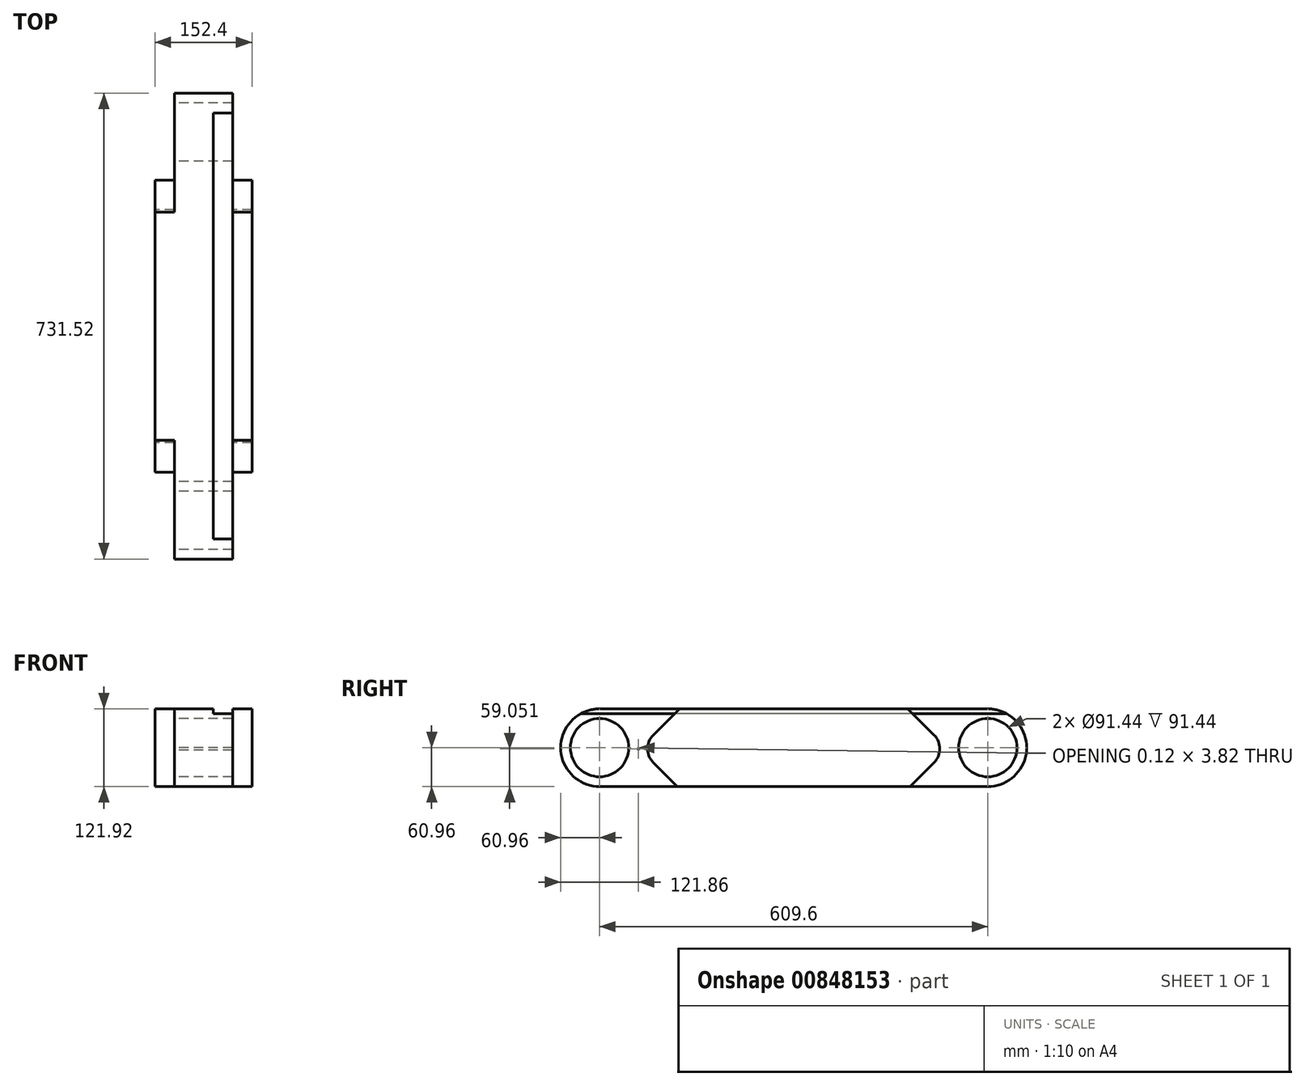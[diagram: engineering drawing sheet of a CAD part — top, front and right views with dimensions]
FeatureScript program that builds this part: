
annotation { "Feature Type Name" : "Feature", "Feature Type Description" : "" }
export const myFeature = defineFeature(function(context is Context, id is Id, definition is map)
    precondition{}
    {
        {
            var Q0;
            Q0=qCreatedBy(makeId("Right.planeOp"),FACE);
            var sketch = newSketch(context, id + "F0", { "sketchPlane" : qUnion([Q0])});
            skCircle(sketch, "E0", {"center": v(0, 0) * mm, "radius": 45.72 * mm});
            skCircle(sketch, "E1", {"center": v(0, 0) * mm, "radius": 60.96 * mm});
            skLineSegment(sketch, "E2.bottom", {"start": v(0, 60.96) * mm, "end": v(-609.6, 60.96) * mm});
            skLineSegment(sketch, "E2.top", {"start": v(0, -60.96) * mm, "end": v(-609.6, -60.96) * mm});
            skLineSegment(sketch, "E2.left", {"start": v(0, 60.96) * mm, "end": v(0, -60.96) * mm});
            skLineSegment(sketch, "E2.right", {"start": v(-609.6, 60.96) * mm, "end": v(-609.6, -60.96) * mm});
            skCircle(sketch, "E3", {"center": v(-609.6, 0) * mm, "radius": 60.96 * mm});
            skCircle(sketch, "E4", {"center": v(-609.6, 0) * mm, "radius": 45.72 * mm});
            skLineSegment(sketch, "E5", {"start": v(-60.96, 0) * mm, "end": v(-60.96, 60.96) * mm});
            skLineSegment(sketch, "E6", {"start": v(-548.64, 0) * mm, "end": v(-548.64, -60.96) * mm});
            skLineSegment(sketch, "E7", {"start": v(-548.76, -3.82) * mm, "end": v(-483.98, 60.96) * mm});
            skLineSegment(sketch, "E8", {"start": v(-548.64, 0) * mm, "end": v(-487.68, -60.96) * mm});
            skLineSegment(sketch, "E9", {"start": v(-304.8, 60.96) * mm, "end": v(-304.8, -60.96) * mm});
            skLineSegment(sketch, "E10.MirrorCS", {"start": v(-60.84, -3.82) * mm, "end": v(-125.62, 60.96) * mm});
            skLineSegment(sketch, "E11.MirrorCS", {"start": v(-60.96, 0) * mm, "end": v(-121.92, -60.96) * mm});
            skSolve(sketch);
        }
        {
            var Q0;
            Q0 = qSketchRegion(id + "F0", true);
            var Q1;
            {var subQ1=sQuery(id+"F0.wireOp",EDGE,"E6");var subQ3=sQuery(id+"F0.wireOp",EDGE,"E7");var subQ4=makeQuery(id+"F0.imprint","INTERSECT",VERTEX,{"derivedFrom":[subQ1,subQ3]});Q1=makeQuery(id+"F0.imprint","IMPRINT",FACE,{"disambiguationData":[TD([[makeQuery(id+"F0.imprint","IMPRINT",EDGE,{"disambiguationData":[TD([[subQ4,-1.0]])],"derivedFrom":subQ3}),1.0]])]});}
            var Q2;
            {var subQ1=sQuery(id+"F0.wireOp",EDGE,"E1");var subQ3=sQuery(id+"F0.wireOp",EDGE,"E10.MirrorCS");var subQ4=makeQuery(id+"F0.imprint","INTERSECT",VERTEX,{"derivedFrom":[subQ1,subQ3]});Q2=makeQuery(id+"F0.imprint","IMPRINT",FACE,{"disambiguationData":[TD([[makeQuery(id+"F0.imprint","IMPRINT",EDGE,{"disambiguationData":[TD([[subQ4,-1.0]])],"derivedFrom":subQ3}),-1.0]])]});}
            extrude(context, id + "F1", {"entities" : qUnion([Q0, Q1, Q2]), "depth" : 91.44 * mm, "offsetDistance" : 30.48 * mm, "symmetric" : true});
        }
        {
            var Q0;
            Q0=qCreatedBy(makeId("Front.planeOp"),FACE);
            var sketch = newSketch(context, id + "F2", { "sketchPlane" : qUnion([Q0])});
            skLineSegment(sketch, "E12.bottom", {"start": v(76.2, 60.96) * mm, "end": v(-76.2, 60.96) * mm});
            skLineSegment(sketch, "E12.top", {"start": v(76.2, -60.96) * mm, "end": v(-76.2, -60.96) * mm});
            skLineSegment(sketch, "E12.left", {"start": v(76.2, 60.96) * mm, "end": v(76.2, -60.96) * mm});
            skLineSegment(sketch, "E12.right", {"start": v(-76.2, 60.96) * mm, "end": v(-76.2, -60.96) * mm});
            skPoint(sketch, "E12.middle", {"position": v(0, 0) * mm});
            skLineSegment(sketch, "E13.bottom", {"start": v(-45.72, 60.96) * mm, "end": v(-15.24, 60.96) * mm});
            skLineSegment(sketch, "E13.top", {"start": v(-45.72, 53.34) * mm, "end": v(-15.24, 53.34) * mm});
            skLineSegment(sketch, "E13.left", {"start": v(-45.72, 60.96) * mm, "end": v(-45.72, 53.34) * mm});
            skLineSegment(sketch, "E13.right", {"start": v(-15.24, 60.96) * mm, "end": v(-15.24, 53.34) * mm});
            skLineSegment(sketch, "E14.bottom", {"start": v(15.24, 53.34) * mm, "end": v(45.72, 53.34) * mm});
            skLineSegment(sketch, "E14.top", {"start": v(15.24, 60.96) * mm, "end": v(45.72, 60.96) * mm});
            skLineSegment(sketch, "E14.left", {"start": v(15.24, 53.34) * mm, "end": v(15.24, 60.96) * mm});
            skLineSegment(sketch, "E14.right", {"start": v(45.72, 53.34) * mm, "end": v(45.72, 60.96) * mm});
            skLineSegment(sketch, "E15", {"start": v(-15.24, 53.34) * mm, "end": v(15.24, 53.34) * mm});
            skLineSegment(sketch, "E16", {"start": v(-76.2, 0) * mm, "end": v(76.2, 0) * mm});
            skLineSegment(sketch, "E17.MirrorCS", {"start": v(15.24, 53.34) * mm, "end": v(-15.24, 53.34) * mm});
            skLineSegment(sketch, "E18.MirrorCS", {"start": v(15.24, 60.96) * mm, "end": v(15.24, 53.34) * mm});
            skLineSegment(sketch, "E19.MirrorCS", {"start": v(15.24, -53.34) * mm, "end": v(-15.24, -53.34) * mm});
            skLineSegment(sketch, "E20.MirrorCS", {"start": v(15.24, -60.96) * mm, "end": v(15.24, -53.34) * mm});
            skLineSegment(sketch, "E21.MirrorCS", {"start": v(-15.24, -53.34) * mm, "end": v(15.24, -53.34) * mm});
            skLineSegment(sketch, "E22.MirrorCS", {"start": v(-45.72, -60.96) * mm, "end": v(-15.24, -60.96) * mm});
            skLineSegment(sketch, "E23.MirrorCS", {"start": v(15.24, -53.34) * mm, "end": v(15.24, -60.96) * mm});
            skLineSegment(sketch, "E24.MirrorCS", {"start": v(15.24, -60.96) * mm, "end": v(45.72, -60.96) * mm});
            skLineSegment(sketch, "E25.MirrorCS", {"start": v(-45.72, -60.96) * mm, "end": v(-45.72, -53.34) * mm});
            skLineSegment(sketch, "E26.MirrorCS", {"start": v(15.24, -53.34) * mm, "end": v(45.72, -53.34) * mm});
            skLineSegment(sketch, "E27.MirrorCS", {"start": v(-45.72, -53.34) * mm, "end": v(-15.24, -53.34) * mm});
            skLineSegment(sketch, "E28.MirrorCS", {"start": v(-15.24, -60.96) * mm, "end": v(-15.24, -53.34) * mm});
            skLineSegment(sketch, "E29.MirrorCS", {"start": v(45.72, -53.34) * mm, "end": v(45.72, -60.96) * mm});
            skSolve(sketch);
        }
        {
            var Q0;
            {var subQ5=sQuery(id+"F0.wireOp",EDGE,"E9");Q0=makeQuery(id+"F0.imprint","IMPRINT",FACE,{"disambiguationData":[TD([[makeQuery(id+"F0.imprint","IMPRINT",EDGE,{"derivedFrom":subQ5}),-1.0]])]});}
            var Q1;
            {var subQ0=sQuery(id+"F0.wireOp",EDGE,"E9");Q1=makeQuery(id+"F0.imprint","IMPRINT",FACE,{"disambiguationData":[TD([[makeQuery(id+"F0.imprint","IMPRINT",EDGE,{"derivedFrom":subQ0}),1.0]])]});}
            extrude(context, id + "F3", {"entities" : qUnion([Q0, Q1]), "operationType" : NewBodyOperationType.ADD, "depth" : 152.4 * mm, "offsetDistance" : 30.48 * mm, "symmetric" : true});
        }
        {
            var Q0;
            Q0=makeQuery(id+"F2.imprint","IMPRINT",FACE,{"disambiguationData":[TD([[makeQuery(id+"F2.imprint","IMPRINT",EDGE,{"derivedFrom":sQuery(id+"F2.wireOp",EDGE,"E13.bottom")}),-1.0]])]});
            var Q1;
            Q1=makeQuery(id+"F2.imprint","IMPRINT",FACE,{"disambiguationData":[TD([[makeQuery(id+"F2.imprint","IMPRINT",EDGE,{"derivedFrom":sQuery(id+"F2.wireOp",EDGE,"E14.bottom")}),1.0]])]});
            var Q2;
            Q2=makeQuery(id+"F2.imprint","IMPRINT",FACE,{"disambiguationData":[TD([[makeQuery(id+"F2.imprint","IMPRINT",EDGE,{"derivedFrom":sQuery(id+"F2.wireOp",EDGE,"E22.MirrorCS")}),1.0]])]});
            var Q3;
            Q3=makeQuery(id+"F2.imprint","IMPRINT",FACE,{"disambiguationData":[TD([[makeQuery(id+"F2.imprint","IMPRINT",EDGE,{"derivedFrom":sQuery(id+"F2.wireOp",EDGE,"E23.MirrorCS")}),1.0]])]});
            extrude(context, id + "F4", {"entities" : qUnion([Q0, Q1, Q2, Q3]), "operationType" : NewBodyOperationType.REMOVE, "oppositeDirection" : true, "depth" : 1524 * mm, "offsetDistance" : 30.48 * mm, "symmetric" : true});
        }
        {
            var Q0;
            {var subQ0=sQuery(id+"F0.wireOp",EDGE,"E7");var subQ1=sQuery(id+"F0.wireOp",EDGE,"E2.top");var subQ2=sQuery(id+"F0.wireOp",EDGE,"E2.bottom");var subQ3=sQuery(id+"F0.wireOp",EDGE,"E8");Q0=makeQuery(id+"F3.boolean.opBoolean","SPLIT",EDGE,{"disambiguationData":[TD([makeQuery(id+"F3.opExtrude","CAP_FACE",FACE,{"disambiguationData":[OSD([subQ2,subQ1,subQ0,subQ3,sQuery(id+"F0.wireOp",EDGE,"E10.MirrorCS"),sQuery(id+"F0.wireOp",EDGE,"E11.MirrorCS")])],"isStart":false})])],"derivedFrom":makeQuery(id+"F3.opExtrude","SWEPT_EDGE",EDGE,{"disambiguationData":[OSD([subQ0,subQ3])]})});}
            var Q1;
            {var subQ0=sQuery(id+"F0.wireOp",EDGE,"E7");var subQ1=sQuery(id+"F0.wireOp",EDGE,"E2.top");var subQ2=sQuery(id+"F0.wireOp",EDGE,"E2.bottom");var subQ3=sQuery(id+"F0.wireOp",EDGE,"E8");Q1=makeQuery(id+"F3.boolean.opBoolean","SPLIT",EDGE,{"disambiguationData":[TD([makeQuery(id+"F3.opExtrude","CAP_FACE",FACE,{"disambiguationData":[OSD([subQ2,subQ1,subQ0,subQ3,sQuery(id+"F0.wireOp",EDGE,"E10.MirrorCS"),sQuery(id+"F0.wireOp",EDGE,"E11.MirrorCS")])],"isStart":true})])],"derivedFrom":makeQuery(id+"F3.opExtrude","SWEPT_EDGE",EDGE,{"disambiguationData":[OSD([subQ0,subQ3])]})});}
            var Q2;
            {var subQ0=sQuery(id+"F0.wireOp",EDGE,"E7");var subQ1=sQuery(id+"F0.wireOp",EDGE,"E2.top");var subQ2=sQuery(id+"F0.wireOp",EDGE,"E2.bottom");var subQ3=sQuery(id+"F0.wireOp",EDGE,"E11.MirrorCS");var subQ4=sQuery(id+"F0.wireOp",EDGE,"E10.MirrorCS");Q2=makeQuery(id+"F3.boolean.opBoolean","SPLIT",EDGE,{"disambiguationData":[TD([makeQuery(id+"F3.opExtrude","CAP_FACE",FACE,{"disambiguationData":[OSD([subQ2,subQ1,subQ0,sQuery(id+"F0.wireOp",EDGE,"E8"),subQ4,subQ3])],"isStart":true})])],"derivedFrom":makeQuery(id+"F3.opExtrude","SWEPT_EDGE",EDGE,{"disambiguationData":[OSD([subQ4,subQ3])]})});}
            var Q3;
            {var subQ0=sQuery(id+"F0.wireOp",EDGE,"E7");var subQ1=sQuery(id+"F0.wireOp",EDGE,"E2.top");var subQ2=sQuery(id+"F0.wireOp",EDGE,"E2.bottom");var subQ3=sQuery(id+"F0.wireOp",EDGE,"E11.MirrorCS");var subQ4=sQuery(id+"F0.wireOp",EDGE,"E10.MirrorCS");Q3=makeQuery(id+"F3.boolean.opBoolean","SPLIT",EDGE,{"disambiguationData":[TD([makeQuery(id+"F3.opExtrude","CAP_FACE",FACE,{"disambiguationData":[OSD([subQ2,subQ1,subQ0,sQuery(id+"F0.wireOp",EDGE,"E8"),subQ4,subQ3])],"isStart":false})])],"derivedFrom":makeQuery(id+"F3.opExtrude","SWEPT_EDGE",EDGE,{"disambiguationData":[OSD([subQ4,subQ3])]})});}
            fillet(context, id + "F5", {"entities" : qUnion([Q0, Q1, Q2, Q3]), "radius" : 30.48 * mm, "tangentPropagation" : true, "allowEdgeOverflow" : false});
        }
    });
